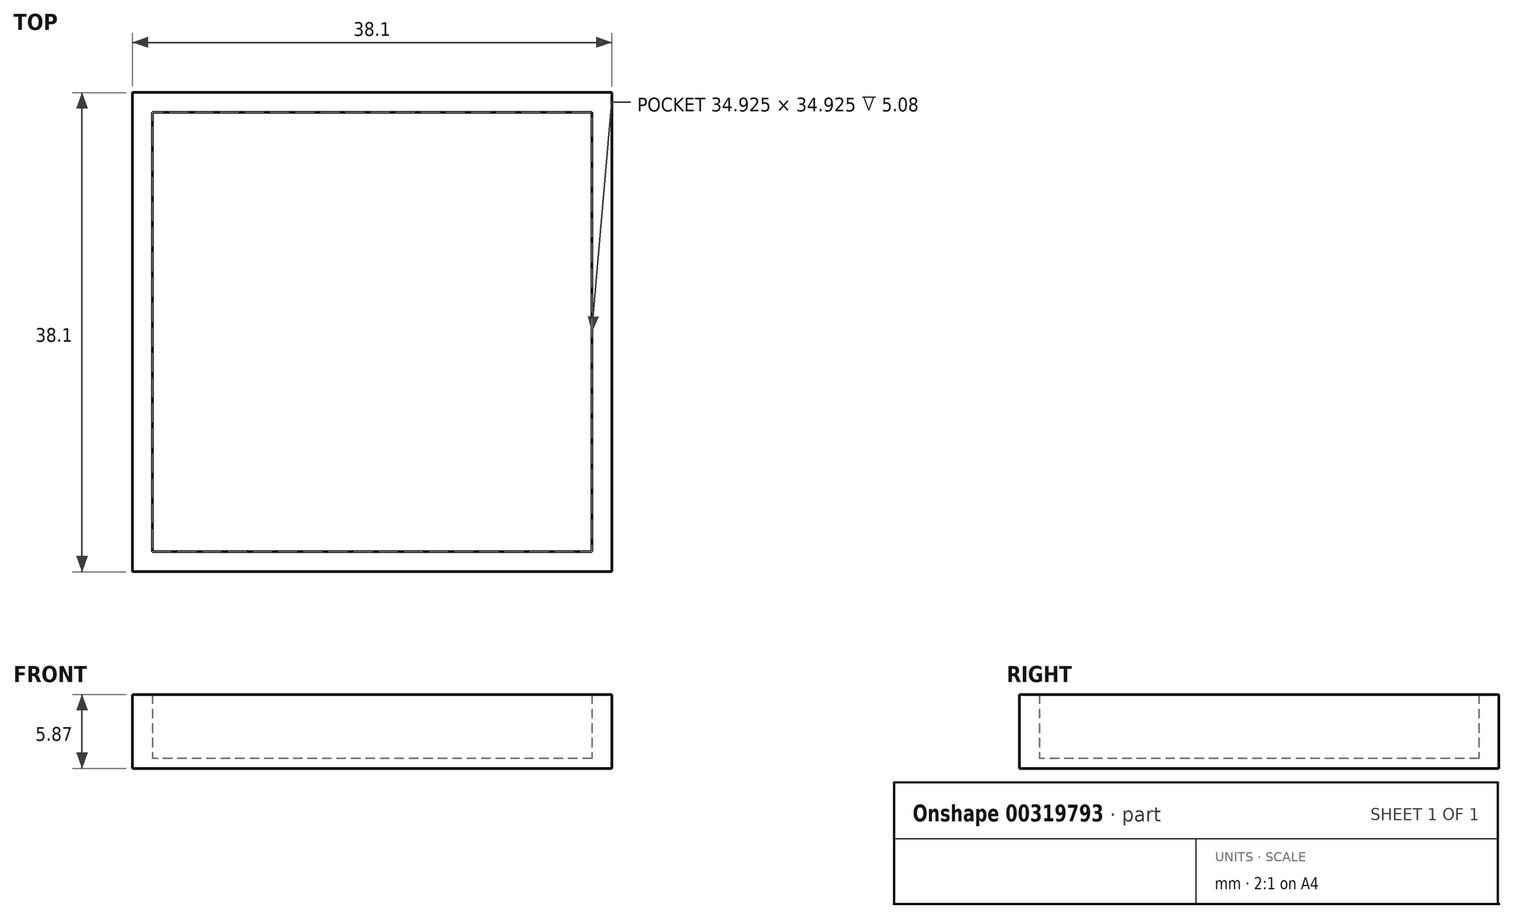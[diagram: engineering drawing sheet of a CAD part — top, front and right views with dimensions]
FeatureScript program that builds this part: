
annotation { "Feature Type Name" : "Feature", "Feature Type Description" : "" }
export const myFeature = defineFeature(function(context is Context, id is Id, definition is map)
    precondition{}
    {
        {
            var Q0;
            Q0=qCreatedBy(makeId("Top.planeOp"),FACE);
            var sketch = newSketch(context, id + "F0", { "sketchPlane" : qUnion([Q0])});
            skLineSegment(sketch, "E0.bottom", {"start": v(-17.9, 26.5) * mm, "end": v(20.2, 26.5) * mm});
            skLineSegment(sketch, "E0.top", {"start": v(-17.9, -11.6) * mm, "end": v(20.2, -11.6) * mm});
            skLineSegment(sketch, "E0.left", {"start": v(-17.9, 26.5) * mm, "end": v(-17.9, -11.6) * mm});
            skLineSegment(sketch, "E0.right", {"start": v(20.2, 26.5) * mm, "end": v(20.2, -11.6) * mm});
            skSolve(sketch);
        }
        {
            var Q0;
            Q0=makeQuery(id+"F0.imprint","IMPRINT",FACE,{"disambiguationData":[TD([[makeQuery(id+"F0.imprint","IMPRINT",EDGE,{"derivedFrom":sQuery(id+"F0.wireOp",EDGE,"E0.bottom")}),-1.0]])]});
            extrude(context, id + "F1", {"entities" : qUnion([Q0]), "depth" : 0.8 * mm});
        }
        {
            var Q0;
            Q0=makeQuery(id+"F1.opExtrude","CAP_FACE",FACE,{"disambiguationData":[OSD([sQuery(id+"F0.wireOp",EDGE,"E0.bottom"),sQuery(id+"F0.wireOp",EDGE,"E0.top"),sQuery(id+"F0.wireOp",EDGE,"E0.left"),sQuery(id+"F0.wireOp",EDGE,"E0.right")])],"isStart":false});
            var sketch = newSketch(context, id + "F2", { "sketchPlane" : qUnion([Q0])});
            skLineSegment(sketch, "E1.0", {"start": v(-16.3, 24.92) * mm, "end": v(-16.3, -10) * mm});
            skLineSegment(sketch, "E1.1", {"start": v(18.62, 24.92) * mm, "end": v(-16.3, 24.92) * mm});
            skLineSegment(sketch, "E1.2", {"start": v(18.62, -10) * mm, "end": v(18.62, 24.92) * mm});
            skLineSegment(sketch, "E1.3", {"start": v(-16.3, -10) * mm, "end": v(18.62, -10) * mm});
            skSolve(sketch);
        }
        {
            var Q0;
            Q0=makeQuery(id+"F2.imprint","IMPRINT",FACE,{"disambiguationData":[TD([[makeQuery(id+"F2.imprint","IMPRINT",EDGE,{"derivedFrom":sQuery(id+"F2.wireOp",EDGE,"E1.0")}),-1.0]])]});
            extrude(context, id + "F3", {"entities" : qUnion([Q0]), "operationType" : NewBodyOperationType.ADD, "depth" : 5.08 * mm});
        }
        {
            var Q0;
            Q0=makeQuery(id+"F1.opExtrude","CAP_FACE",FACE,{"disambiguationData":[OSD([sQuery(id+"F0.wireOp",EDGE,"E0.bottom"),sQuery(id+"F0.wireOp",EDGE,"E0.top"),sQuery(id+"F0.wireOp",EDGE,"E0.left"),sQuery(id+"F0.wireOp",EDGE,"E0.right")])],"isStart":false});
            var sketch = newSketch(context, id + "F4", { "sketchPlane" : qUnion([Q0])});
            skLineSegment(sketch, "E2.bottom", {"start": v(-9.96, -10) * mm, "end": v(-11.23, -10) * mm});
            skLineSegment(sketch, "E2.top", {"start": v(-9.96, 19.84) * mm, "end": v(-11.23, 19.84) * mm});
            skLineSegment(sketch, "E2.left", {"start": v(-9.96, -10) * mm, "end": v(-9.96, -4.93) * mm});
            skLineSegment(sketch, "E2.right", {"start": v(-11.23, -10) * mm, "end": v(-11.23, 19.84) * mm});
            skLineSegment(sketch, "E3.bottom", {"start": v(-9.96, 19.84) * mm, "end": v(12.27, 19.84) * mm});
            skLineSegment(sketch, "E3.top", {"start": v(-9.96, 18.57) * mm, "end": v(-4.88, 18.57) * mm});
            skLineSegment(sketch, "E3.right", {"start": v(12.27, 19.84) * mm, "end": v(12.27, 18.57) * mm});
            skLineSegment(sketch, "E4.bottom", {"start": v(18.62, 7.45) * mm, "end": v(13.54, 7.45) * mm});
            skLineSegment(sketch, "E4.top", {"start": v(18.62, 8.72) * mm, "end": v(10.8, 8.72) * mm});
            skLineSegment(sketch, "E4.left", {"start": v(18.62, 7.45) * mm, "end": v(18.62, 8.72) * mm});
            skLineSegment(sketch, "E4.right", {"start": v(1.47, 7.45) * mm, "end": v(1.47, 8.72) * mm});
            skPoint(sketch, "E5.firstSnap0", {"position": v(10.04, 7.45) * mm});
            skLineSegment(sketch, "E5.top", {"start": v(12.27, -10) * mm, "end": v(13.54, -10) * mm});
            skLineSegment(sketch, "E5.left", {"start": v(12.27, 7.45) * mm, "end": v(12.27, -10) * mm});
            skLineSegment(sketch, "E5.right", {"start": v(13.54, 7.45) * mm, "end": v(13.54, -10) * mm});
            skLineSegment(sketch, "E6.top", {"start": v(-4.88, 0.81) * mm, "end": v(-3.6, 0.81) * mm});
            skLineSegment(sketch, "E6.left", {"start": v(-4.88, 18.57) * mm, "end": v(-4.88, 9.05) * mm});
            skLineSegment(sketch, "E6.right", {"start": v(-3.6, 18.57) * mm, "end": v(-3.6, 12.86) * mm});
            skLineSegment(sketch, "E7.bottom", {"start": v(-4.88, 9.05) * mm, "end": v(-4.88, 9.05) * mm});
            skLineSegment(sketch, "E7.top", {"start": v(-4.88, 7.78) * mm, "end": v(-4.88, 7.78) * mm});
            skLineSegment(sketch, "E7.left", {"start": v(-4.88, 9.05) * mm, "end": v(-4.88, 7.78) * mm});
            skLineSegment(sketch, "E8.bottom", {"start": v(-3.6, 2.37) * mm, "end": v(7.19, 2.37) * mm});
            skLineSegment(sketch, "E8.top", {"start": v(-3.6, 1.1) * mm, "end": v(7.19, 1.1) * mm});
            skLineSegment(sketch, "E8.right", {"start": v(7.19, 2.37) * mm, "end": v(7.19, 1.1) * mm});
            skLineSegment(sketch, "E9.top", {"start": v(10.8, 13) * mm, "end": v(9.53, 13) * mm});
            skLineSegment(sketch, "E9.left", {"start": v(10.8, 8.72) * mm, "end": v(10.8, 13) * mm});
            skLineSegment(sketch, "E9.right", {"start": v(9.53, 8.72) * mm, "end": v(9.53, 13) * mm});
            skLineSegment(sketch, "E10.trimOffspring", {"start": v(-3.6, 18.57) * mm, "end": v(12.27, 18.57) * mm});
            skLineSegment(sketch, "E11.trimOffspring", {"start": v(-4.88, 7.78) * mm, "end": v(-4.88, 0.81) * mm});
            skLineSegment(sketch, "E12.trimOffspring", {"start": v(-3.6, 7.78) * mm, "end": v(-3.6, 2.37) * mm});
            skLineSegment(sketch, "E13.trimOffspring", {"start": v(-3.6, 1.1) * mm, "end": v(-3.6, 0.81) * mm});
            skLineSegment(sketch, "E14.trimOffspring", {"start": v(9.53, 8.72) * mm, "end": v(1.47, 8.72) * mm});
            skLineSegment(sketch, "E15.trimOffspring", {"start": v(12.27, 7.45) * mm, "end": v(1.47, 7.45) * mm});
            skLineSegment(sketch, "E16.trimOffspring", {"start": v(-9.96, -3.98) * mm, "end": v(-9.96, 18.57) * mm});
            skLineSegment(sketch, "E17", {"start": v(-3.6, 7.78) * mm, "end": v(-3.6, 12.86) * mm});
            skLineSegment(sketch, "E18", {"start": v(-16.3, -10) * mm, "end": v(-11.23, -10) * mm});
            skCircle(sketch, "E19", {"center": v(-13.77, -6.22) * mm, "radius": 1.27 * mm});
            skPoint(sketch, "E19.centerSnap0", {"position": v(-13.77, -10) * mm});
            skCircle(sketch, "E20", {"center": v(-7.42, 13.66) * mm, "radius": 1.27 * mm});
            skPoint(sketch, "E20.centerSnap0", {"position": v(-7.42, 18.57) * mm});
            skLineSegment(sketch, "E21", {"start": v(-9.96, -3.98) * mm, "end": v(-9.96, -4.93) * mm});
            skSolve(sketch);
        }
        {
            var Q0;
            Q0=sQuery(id+"F4.wireOp",EDGE,"E10.trimOffspring");
            var Q1;
            Q1=sQuery(id+"F4.wireOp",EDGE,"E3.bottom");
            var Q2;
            Q2=sQuery(id+"F4.wireOp",EDGE,"E3.right");
            var Q3;
            Q3=sQuery(id+"F4.wireOp",EDGE,"E2.top");
            var Q4;
            Q4=sQuery(id+"F4.wireOp",EDGE,"E2.right");
            var Q5;
            Q5=sQuery(id+"F4.wireOp",EDGE,"E16.trimOffspring");
            var Q6;
            Q6=sQuery(id+"F4.wireOp",EDGE,"E2.left");
            var Q7;
            Q7=sQuery(id+"F4.wireOp",EDGE,"E3.top");
            var Q8;
            Q8=sQuery(id+"F4.wireOp",EDGE,"E6.left");
            var Q9;
            Q9=sQuery(id+"F4.wireOp",EDGE,"E7.left");
            var Q10;
            Q10=sQuery(id+"F4.wireOp",EDGE,"E11.trimOffspring");
            var Q11;
            Q11=sQuery(id+"F4.wireOp",EDGE,"E6.top");
            var Q12;
            Q12=sQuery(id+"F4.wireOp",EDGE,"E8.right");
            var Q13;
            Q13=sQuery(id+"F4.wireOp",EDGE,"E8.top");
            var Q14;
            Q14=sQuery(id+"F4.wireOp",EDGE,"E8.bottom");
            var Q15;
            Q15=sQuery(id+"F4.wireOp",EDGE,"E12.trimOffspring");
            var Q16;
            Q16=sQuery(id+"F4.wireOp",EDGE,"E17");
            var Q17;
            Q17=sQuery(id+"F4.wireOp",EDGE,"E6.right");
            var Q18;
            Q18=sQuery(id+"F4.wireOp",EDGE,"E14.trimOffspring");
            var Q19;
            Q19=sQuery(id+"F4.wireOp",EDGE,"E15.trimOffspring");
            var Q20;
            Q20=sQuery(id+"F4.wireOp",EDGE,"E4.right");
            var Q21;
            Q21=sQuery(id+"F4.wireOp",EDGE,"E9.top");
            var Q22;
            Q22=sQuery(id+"F4.wireOp",EDGE,"E9.right");
            var Q23;
            Q23=sQuery(id+"F4.wireOp",EDGE,"E9.left");
            var Q24;
            Q24=sQuery(id+"F4.wireOp",EDGE,"E4.top");
            var Q25;
            Q25=sQuery(id+"F4.wireOp",EDGE,"E4.bottom");
            var Q26;
            Q26=sQuery(id+"F4.wireOp",EDGE,"E5.right");
            var Q27;
            Q27=sQuery(id+"F4.wireOp",EDGE,"E5.left");
            var Q28;
            Q28=sQuery(id+"F4.wireOp",EDGE,"E4.left");
            extrude(context, id + "F5", {"bodyType" : ToolBodyType.SURFACE, "surfaceEntities" : qUnion([Q0, Q1, Q2, Q3, Q4, Q5, Q6, Q7, Q8, Q9, Q10, Q11, Q12, Q13, Q14, Q15, Q16, Q17, Q18, Q19, Q20, Q21, Q22, Q23, Q24, Q25, Q26, Q27, Q28]), "depth" : -2.13 * mm});
        }
        {
            var Q0;
            Q0=sQuery(id+"F4.wireOp",EDGE,"E19");
            extrude(context, id + "F6", {"bodyType" : ToolBodyType.SURFACE, "operationType" : NewBodyOperationType.REMOVE, "surfaceEntities" : qUnion([Q0]), "oppositeDirection" : true, "depth" : 0.4 * mm});
        }
    });
